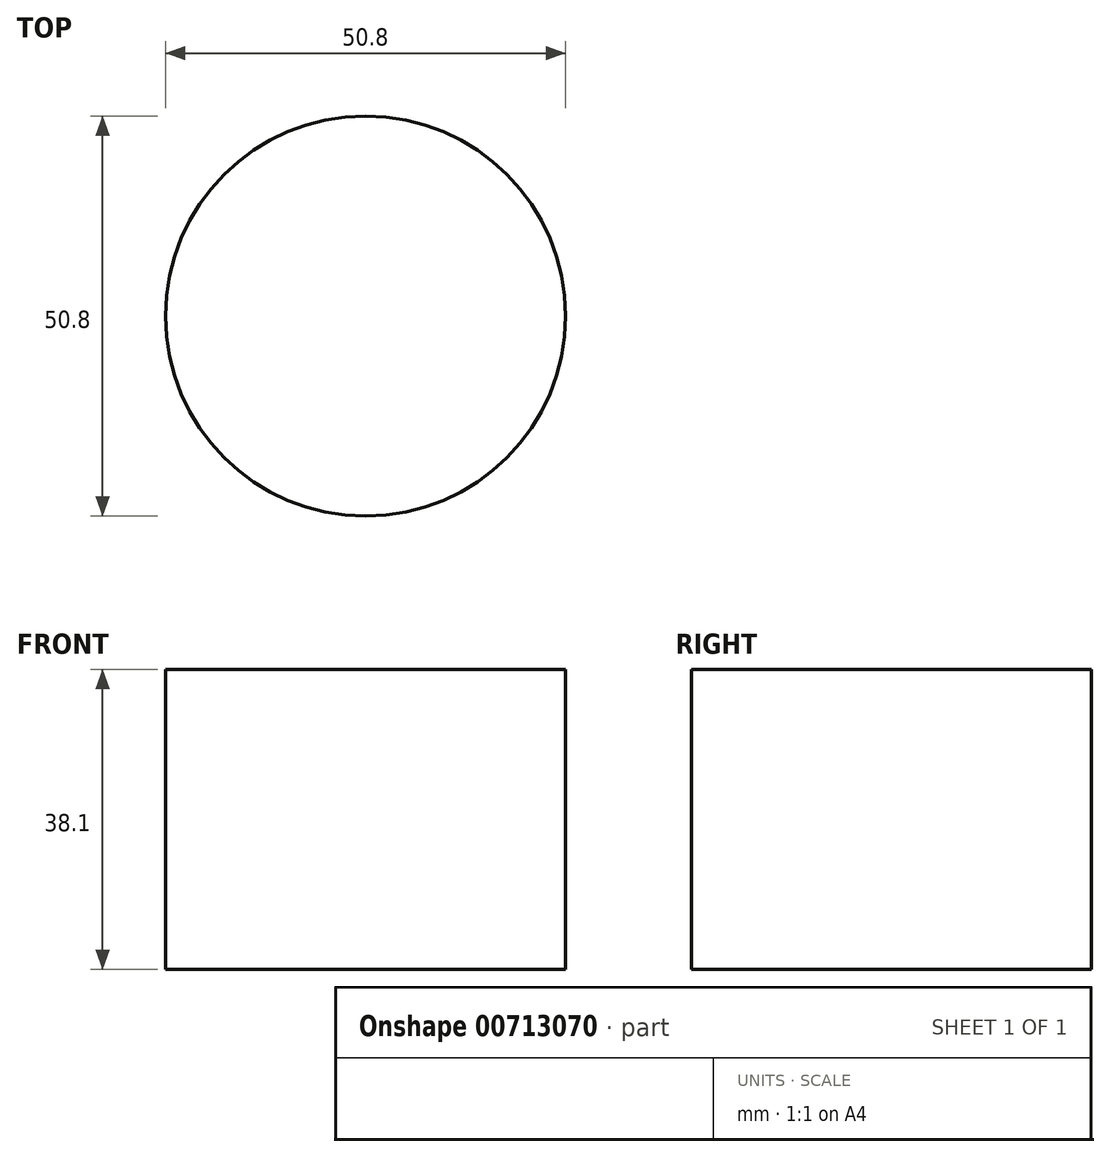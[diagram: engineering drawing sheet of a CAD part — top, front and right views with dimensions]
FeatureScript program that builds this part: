
annotation { "Feature Type Name" : "Feature", "Feature Type Description" : "" }
export const myFeature = defineFeature(function(context is Context, id is Id, definition is map)
    precondition{}
    {
        {
            var Q0;
            Q0=qCreatedBy(makeId("Top.planeOp"),FACE);
            var sketch = newSketch(context, id + "F0", { "sketchPlane" : qUnion([Q0])});
            skCircle(sketch, "E0", {"center": v(0, 0) * mm, "radius": 25.4 * mm});
            skSolve(sketch);
        }
        {
            var Q0;
            Q0=makeQuery(id+"F0.imprint","IMPRINT",FACE,{"disambiguationData":[TD([[makeQuery(id+"F0.imprint","IMPRINT",EDGE,{"derivedFrom":sQuery(id+"F0.wireOp",EDGE,"E0")}),1.0]])]});
            extrude(context, id + "F1", {"entities" : qUnion([Q0]), "depth" : 38.1 * mm, "offsetDistance" : 25.4 * mm});
        }
    });
